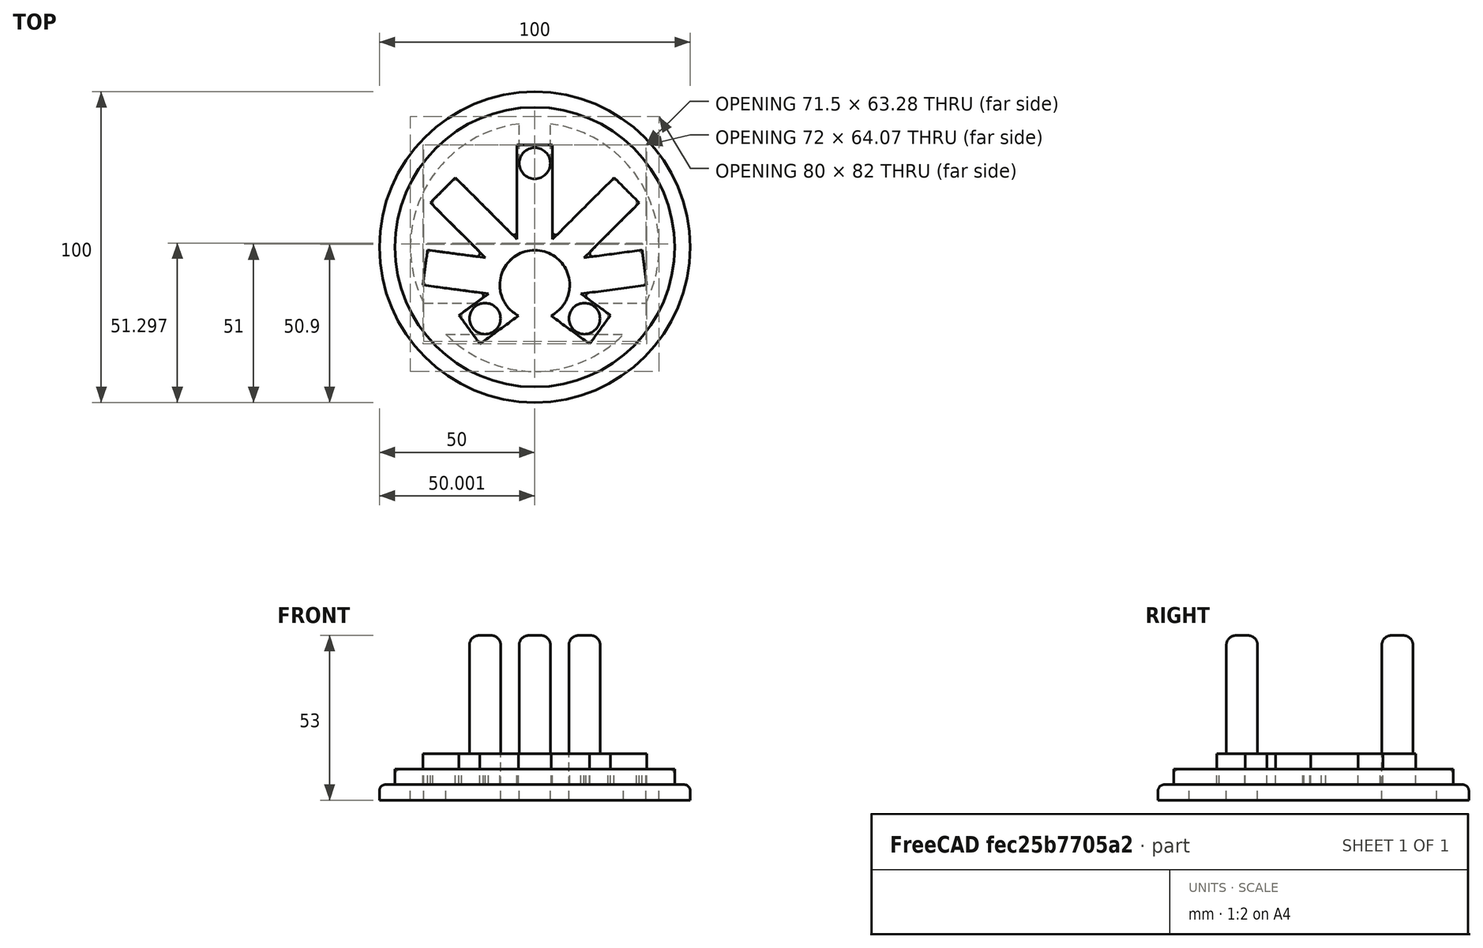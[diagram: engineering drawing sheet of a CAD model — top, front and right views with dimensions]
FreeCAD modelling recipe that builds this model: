
FCSTD DOCUMENT  (FreeCAD 0.16R6712 (Git))
Label: leaf-coaster
License: All rights reserved
LicenseURL: http://en.wikipedia.org/wiki/All_rights_reserved
objects: Part::Fillet×7, Part::Cylinder×5, Part::MultiFuse×4, Part::Cut×3, Part::Box×3, Part::Extrusion×2, Part::Feature×1
note: 25 computed .brp shape members not serialized (recipe doc carries the construction recipe); baked Part::Feature solids carry a one-line shape summary decoded from their .brp

FEATURE [Part::Cylinder] Cylinder
  Angle = 360
  Height = 5
  Radius = 45
FEATURE [Part::Feature] Face001
  shape: bbox 72 x 64.07 x 2e-07 mm, 1 faces, 0 solids (baked)
FEATURE [Part::Extrusion] Extrude
  Base = -> Face001
  Dir = (0,0,10)
  Solid = false
FEATURE [Part::Extrusion] Extrude002
  Base = -> Face001
  Dir = (0,0,10)
  Solid = false
FEATURE [Part::Cut] Cut
  Base = -> Cylinder
  Tool = -> Extrude
FEATURE [Part::Cut] Cut001
  Base = -> Cylinder
  Tool = -> Extrude
FEATURE [Part::Fillet] Fillet
  Base = -> Cut
  Edges = 14 edges r=2: [Edge57,Edge58,Edge60,Edge61,Edge63,Edge64,Edge66,Edge67,Edge69,Edge70,Edge72,Edge73,Edge75,Edge76]
FEATURE [Part::Fillet] Fillet001
  Base = -> Fillet
  Edges = 1 edges r=2: [Edge40]
FEATURE [Part::Fillet] Fillet002  label="Coaster"
  Base = -> Fillet001
  Edges = 6 edges r=1: [Edge59,Edge79,Edge81,Edge99,Edge101,Edge119]
FEATURE [Part::Cylinder] Cylinder001
  Angle = 360
  Height = 5
  Placement = pos=(0,0,-5) rot=(0,0,1;0rad)
  Radius = 50
FEATURE [Part::Fillet] Fillet003
  Base = -> Cylinder001
  Edges = 1 edges r=2: [Edge1]
FEATURE [Part::Cylinder] Cylinder002
  Angle = 360
  Height = 53
  Placement = pos=(0,27,-5) rot=(0,0,1;0rad)
  Radius = 5
FEATURE [Part::Cylinder] Cylinder003
  Angle = 360
  Height = 53
  Placement = pos=(-16,-23,-5) rot=(0,0,1;0rad)
  Radius = 5
FEATURE [Part::Cylinder] Cylinder005
  Angle = 360
  Height = 10
  Placement = pos=(0,0,-7) rot=(0,0,1;0rad)
  Radius = 40
FEATURE [Part::Cut] Cut002
  Base = -> Fillet003
  Tool = -> Cylinder005
FEATURE [Part::Box] Box  label="Cube"
  Height = 5
  Length = 10
  Placement = pos=(-5,27,-5) rot=(0,0,1;0rad)
  Width = 15
FEATURE [Part::Fillet] Fillet004
  Base = -> Cylinder002
  Edges = 1 edges r=3: [Edge1]
FEATURE [Part::Fillet] Fillet005
  Base = -> Cylinder003
  Edges = 1 edges r=3: [Edge1]
FEATURE [Part::Fillet] Fillet006
  Edges = 1 edges r=3: [Edge1]
FEATURE [Part::Box] Box001  label="Cube001"
  Height = 5
  Length = 20
  Placement = pos=(16,-28,-5) rot=(0,0,1;0rad)
  Width = 10
FEATURE [Part::Box] Box002  label="Cube002"
  Height = 5
  Length = 20
  Placement = pos=(-36,-28,-5) rot=(0,0,1;0rad)
  Width = 10
FEATURE [Part::MultiFuse] Fusion
  Shapes = -> [Fillet005,Box002]
FEATURE [Part::MultiFuse] Fusion001
  Shapes = -> [Fillet006,Box001]
FEATURE [Part::MultiFuse] Fusion002
  Shapes = -> [Box,Fillet004]
FEATURE [Part::MultiFuse] Fusion003  label="Holder"
  Shapes = -> [Cut002,Fusion,Fusion001,Fusion002]
